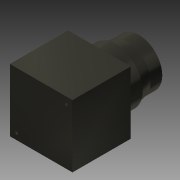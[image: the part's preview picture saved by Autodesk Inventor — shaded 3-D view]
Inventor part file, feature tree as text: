
AUTODESK INVENTOR PART (.ipt)
format: ipt  version: 2013 (Build 170138000, 138)  size: 141,312 bytes
history: native  units: mm
features: sketch x7, extrude x6, chamfer x1, hole x1, fillet x1
ambient origin geometry x8: Origin, YZ Plane, XZ Plane, XY Plane, X Axis, Y Axis, Z Axis, Center Point
bodies: Solid1 (feature_tree)
feature tree (16):
  extrude  "Extrusion1"  Depth=48.4mm
  extrude  "Extrusion2"  Depth=42.0mm
  extrude  "Extrusion3"  Depth=9.0mm TaperAngle=0.0deg
  chamfer  "Chamfer1"  Distance=2.0mm Angle=45.0deg
  extrude  "Extrusion4"  Depth=9.0mm
  extrude  "Extrusion5"  Depth=20.0mm TaperAngle=0.0deg
  hole  "Hole1"  [1 undecoded]
  extrude  "Extrusion6"  Depth=5.0mm
  fillet  "Fillet1"  Radius=5.0mm
  sketch  "Sketch1"  dims[d0=48.4mm d2=48.4mm]
  sketch  "Sketch2"  dims[d3=45.0mm d4=0.0mm d5=42.0mm]
  sketch  "Sketch3"  dims[d7=12.5mm d8=0.0mm d9=9.0mm d10=0.0mm d11=2.0mm d12=9.0mm d13=45.0deg]
  sketch  "Sketch4"  dims[d14=9.0mm d15=0.0mm d16=9.0mm]
  sketch  "Sketch5"  dims[d18=4.5mm d19=20.0mm d20=0.0mm]
  sketch  "Sketch6"  dims[d21=5.0mm d22=5.0mm]
  sketch  "Sketch7"  dims[d23=5.0mm d24=5.0mm d25=2.5mm d26=6.0mm d27=4.0mm d28=2.0mm d29=90.0deg d30=8.0mm d31=20.594885mm d32=5.0mm d33=0.0mm d34=2.0mm]
note: 1 required parameter value undecoded (feature->parameter linkage not recoverable at this tier; creation-order binding heuristic only, values carry confidence <= 0.55)
